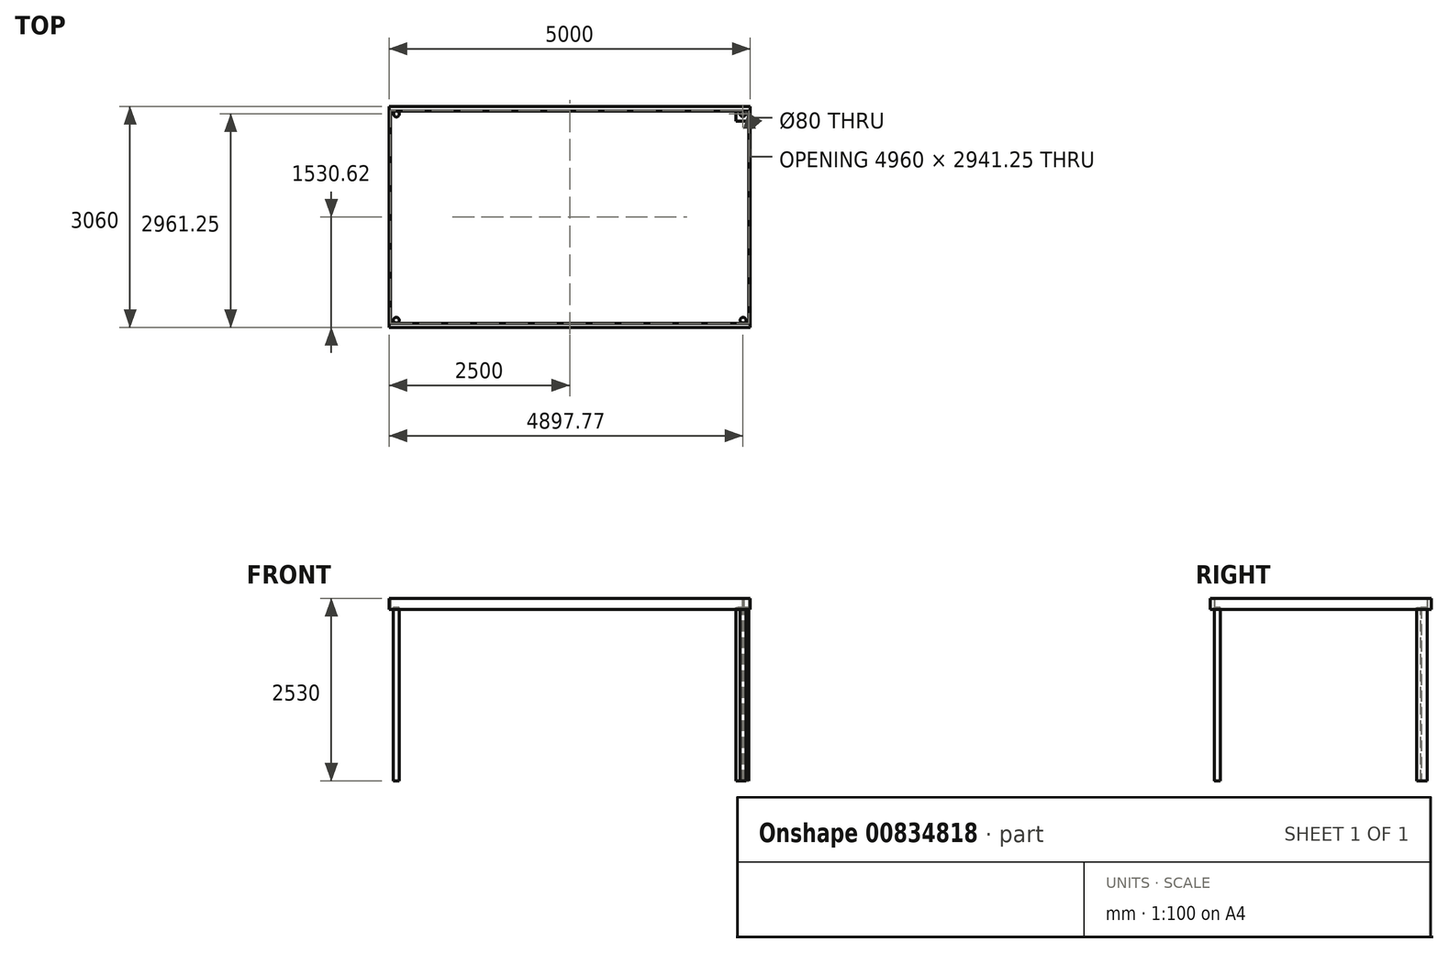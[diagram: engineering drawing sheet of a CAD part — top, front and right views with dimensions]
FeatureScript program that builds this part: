
annotation { "Feature Type Name" : "Feature", "Feature Type Description" : "" }
export const myFeature = defineFeature(function(context is Context, id is Id, definition is map)
    precondition{}
    {
        {
            var Q0;
            Q0=qCreatedBy(makeId("Top.planeOp"),FACE);
            var sketch = newSketch(context, id + "F0", { "sketchPlane" : qUnion([Q0])});
            skLineSegment(sketch, "E0.bottom", {"start": v(-2500, 30) * mm, "end": v(2500, 30) * mm});
            skLineSegment(sketch, "E0.top", {"start": v(-2500, -30) * mm, "end": v(2500, -30) * mm});
            skLineSegment(sketch, "E0.left", {"start": v(-2500, 30) * mm, "end": v(-2500, -30) * mm});
            skLineSegment(sketch, "E0.right", {"start": v(2500, 30) * mm, "end": v(2500, -30) * mm});
            skPoint(sketch, "E0.middle", {"position": v(0, 0) * mm});
            skLineSegment(sketch, "E1.bottom", {"start": v(-2500, 30) * mm, "end": v(-2480, 30) * mm});
            skLineSegment(sketch, "E1.top", {"start": v(-2500, 3030) * mm, "end": v(-2480, 3030) * mm});
            skLineSegment(sketch, "E1.left", {"start": v(-2500, 30) * mm, "end": v(-2500, 3030) * mm});
            skLineSegment(sketch, "E1.right", {"start": v(-2480, 30) * mm, "end": v(-2480, 3030) * mm});
            skLineSegment(sketch, "E2.bottom", {"start": v(-2480, 3030) * mm, "end": v(2500, 3030) * mm});
            skLineSegment(sketch, "E2.top", {"start": v(-2480, 2970) * mm, "end": v(2500, 2970) * mm});
            skLineSegment(sketch, "E2.left", {"start": v(-2480, 3030) * mm, "end": v(-2480, 2970) * mm});
            skLineSegment(sketch, "E2.right", {"start": v(2500, 3030) * mm, "end": v(2500, 2970) * mm});
            skLineSegment(sketch, "E3.bottom", {"start": v(2500, 2970) * mm, "end": v(2480, 2970) * mm});
            skLineSegment(sketch, "E3.top", {"start": v(2500, 30) * mm, "end": v(2480, 30) * mm});
            skLineSegment(sketch, "E3.left", {"start": v(2500, 2970) * mm, "end": v(2500, 30) * mm});
            skLineSegment(sketch, "E3.right", {"start": v(2480, 2970) * mm, "end": v(2480, 30) * mm});
            skLineSegment(sketch, "E4.bottom", {"start": v(-2500, 3030) * mm, "end": v(-2300, 3030) * mm});
            skLineSegment(sketch, "E4.top", {"start": v(-2500, 2830) * mm, "end": v(-2300, 2830) * mm});
            skLineSegment(sketch, "E4.left", {"start": v(-2500, 3030) * mm, "end": v(-2500, 2830) * mm});
            skLineSegment(sketch, "E4.right", {"start": v(-2300, 3030) * mm, "end": v(-2300, 2830) * mm});
            skLineSegment(sketch, "E5.bottom", {"start": v(-2500, -30) * mm, "end": v(-2300, -30) * mm});
            skLineSegment(sketch, "E5.top", {"start": v(-2500, 177.46) * mm, "end": v(-2300, 177.46) * mm});
            skLineSegment(sketch, "E5.left", {"start": v(-2500, -30) * mm, "end": v(-2500, 177.46) * mm});
            skLineSegment(sketch, "E5.right", {"start": v(-2300, -30) * mm, "end": v(-2300, 177.46) * mm});
            skLineSegment(sketch, "E6.bottom", {"start": v(2500, 3030) * mm, "end": v(2300, 3030) * mm});
            skLineSegment(sketch, "E6.top", {"start": v(2500, 2830) * mm, "end": v(2300, 2830) * mm});
            skLineSegment(sketch, "E6.left", {"start": v(2500, 3030) * mm, "end": v(2500, 2830) * mm});
            skLineSegment(sketch, "E6.right", {"start": v(2300, 3030) * mm, "end": v(2300, 2830) * mm});
            skLineSegment(sketch, "E7.bottom", {"start": v(2500, -30) * mm, "end": v(2300, -30) * mm});
            skLineSegment(sketch, "E7.top", {"start": v(2500, 170) * mm, "end": v(2300, 170) * mm});
            skLineSegment(sketch, "E7.left", {"start": v(2500, -30) * mm, "end": v(2500, 170) * mm});
            skLineSegment(sketch, "E7.right", {"start": v(2300, -30) * mm, "end": v(2300, 170) * mm});
            skPoint(sketch, "E8", {"position": v(-2500, 2930) * mm});
            skPoint(sketch, "E9", {"position": v(2500, 2930) * mm});
            skPoint(sketch, "E10", {"position": v(2300, 2930) * mm});
            skPoint(sketch, "E11", {"position": v(2400, 2830) * mm});
            skPoint(sketch, "E12", {"position": v(2400, 3030) * mm});
            skPoint(sketch, "E13", {"position": v(2400.25, 2930) * mm});
            skPoint(sketch, "E14", {"position": v(-2300, 2930) * mm});
            skPoint(sketch, "E15", {"position": v(-2400, 2830) * mm});
            skPoint(sketch, "E16", {"position": v(-2400, 3030) * mm});
            skPoint(sketch, "E17", {"position": v(-2399.75, 2930) * mm});
            skPoint(sketch, "E18", {"position": v(-2500, 73.73) * mm});
            skPoint(sketch, "E19", {"position": v(-2300, 73.73) * mm});
            skPoint(sketch, "E20", {"position": v(-2400, 177.46) * mm});
            skPoint(sketch, "E21", {"position": v(-2400, -30) * mm});
            skPoint(sketch, "E22", {"position": v(-2398.07, 73.73) * mm});
            skPoint(sketch, "E23", {"position": v(2300, 70) * mm});
            skPoint(sketch, "E24", {"position": v(2500, 70) * mm});
            skPoint(sketch, "E25", {"position": v(2400, 170) * mm});
            skPoint(sketch, "E26", {"position": v(2400, -30) * mm});
            skPoint(sketch, "E27", {"position": v(2397.77, 68.75) * mm});
            skCircle(sketch, "E28", {"center": v(-2399.75, 2930) * mm, "radius": 40 * mm});
            skCircle(sketch, "E29", {"center": v(-2398.07, 73.73) * mm, "radius": 40 * mm});
            skCircle(sketch, "E30", {"center": v(2397.77, 68.75) * mm, "radius": 40 * mm});
            skCircle(sketch, "E31", {"center": v(2400.25, 2930) * mm, "radius": 40 * mm});
            skLineSegment(sketch, "E32", {"start": v(-2500, 1530) * mm, "end": v(2500, 1530) * mm});
            skPoint(sketch, "E32.endSnap0", {"position": v(-2480, 1530) * mm});
            skSolve(sketch);
        }
        {
            var Q0;
            Q0 = qSketchRegion(id + "F0", true);
            extrude(context, id + "F1", {"entities" : qUnion([Q0]), "oppositeDirection" : true, "depth" : 130 * mm, "offsetDistance" : 25 * mm});
        }
        {
            var Q0;
            Q0 = qSketchRegion(id + "F0", true);
            extrude(context, id + "F2", {"entities" : qUnion([Q0]), "operationType" : NewBodyOperationType.ADD, "depth" : 25 * mm, "offsetDistance" : 25 * mm});
        }
        {
            var Q0;
            Q0=makeQuery(id+"F0.imprint","IMPRINT",FACE,{"disambiguationData":[TD([[makeQuery(id+"F0.imprint","IMPRINT",EDGE,{"derivedFrom":sQuery(id+"F0.wireOp",EDGE,"E31")}),1.0]])]});
            var Q1;
            {var subQ0=sQuery(id+"F0.wireOp",EDGE,"E30");var subQ1=sQuery(id+"F0.wireOp",EDGE,"E0.bottom");var subQ2=makeQuery(id+"F0.imprint","INTERSECT",VERTEX,{"disambiguationData":[OD(0.0)],"derivedFrom":[subQ1,subQ0]});Q1=makeQuery(id+"F0.imprint","IMPRINT",FACE,{"disambiguationData":[TD([[makeQuery(id+"F0.imprint","IMPRINT",EDGE,{"disambiguationData":[TD([[subQ2,-1.0]])],"derivedFrom":subQ1}),1.0]])]});}
            var Q2;
            Q2=makeQuery(id+"F0.imprint","IMPRINT",FACE,{"disambiguationData":[TD([[makeQuery(id+"F0.imprint","IMPRINT",EDGE,{"derivedFrom":sQuery(id+"F0.wireOp",EDGE,"E29")}),1.0]])]});
            var Q3;
            Q3=makeQuery(id+"F0.imprint","IMPRINT",FACE,{"disambiguationData":[TD([[makeQuery(id+"F0.imprint","IMPRINT",EDGE,{"derivedFrom":sQuery(id+"F0.wireOp",EDGE,"E28")}),1.0]])]});
            extrude(context, id + "F3", {"entities" : qUnion([Q0, Q1, Q2, Q3]), "operationType" : NewBodyOperationType.ADD, "depth" : 2400 * mm, "offsetDistance" : 25 * mm});
        }
        {
            var Q0;
            Q0=makeQuery(id+"F1.opExtrude","SWEPT_BODY",BODY,{"disambiguationData":[OSD([sQuery(id+"F0.wireOp",EDGE,"E0.bottom"),sQuery(id+"F0.wireOp",EDGE,"E0.top"),sQuery(id+"F0.wireOp",EDGE,"E1.left"),sQuery(id+"F0.wireOp",EDGE,"E1.right"),sQuery(id+"F0.wireOp",EDGE,"E2.bottom"),sQuery(id+"F0.wireOp",EDGE,"E2.top"),sQuery(id+"F0.wireOp",EDGE,"E3.left"),sQuery(id+"F0.wireOp",EDGE,"E3.right"),sQuery(id+"F0.wireOp",EDGE,"E4.bottom"),sQuery(id+"F0.wireOp",EDGE,"E4.left"),sQuery(id+"F0.wireOp",EDGE,"E5.bottom"),sQuery(id+"F0.wireOp",EDGE,"E5.left"),sQuery(id+"F0.wireOp",EDGE,"E6.bottom"),sQuery(id+"F0.wireOp",EDGE,"E6.left"),sQuery(id+"F0.wireOp",EDGE,"E7.bottom"),sQuery(id+"F0.wireOp",EDGE,"E7.left"),sQuery(id+"F0.wireOp",EDGE,"E30")])]});
            var Q1;
            Q1=makeQuery(id+"F3.opExtrude","SWEPT_BODY",BODY,{"disambiguationData":[OSD([sQuery(id+"F0.wireOp",EDGE,"E31")])]});
            var Q2;
            Q2=makeQuery(id+"F3.opExtrude","SWEPT_BODY",BODY,{"disambiguationData":[OSD([sQuery(id+"F0.wireOp",EDGE,"E29")])]});
            var Q3;
            Q3=makeQuery(id+"F3.opExtrude","SWEPT_BODY",BODY,{"disambiguationData":[OSD([sQuery(id+"F0.wireOp",EDGE,"E28")])]});
            var Q4;
            Q4=makeQuery(id+"F3.opExtrude","SWEPT_BODY",BODY,{"disambiguationData":[OSD([sQuery(id+"F0.wireOp",EDGE,"E0.bottom"),sQuery(id+"F0.wireOp",EDGE,"E30")])]});
            var Q5;
            Q5=sQuery(id+"F0.wireOp",EDGE,"E32");
            var Q6;
            Q6=sQuery(id+"F0.wireOp",EDGE,"E32");
            transform(context, id + "F4", {"entities" : qUnion([Q0, Q1, Q2, Q3, Q4]), "transformType" : TransformType.ROTATION, "transformAxis" : qUnion([Q6]), "angle" : 180 * degree, "oppositeDirection" : true, "makeCopy" : false});
        }
    });
